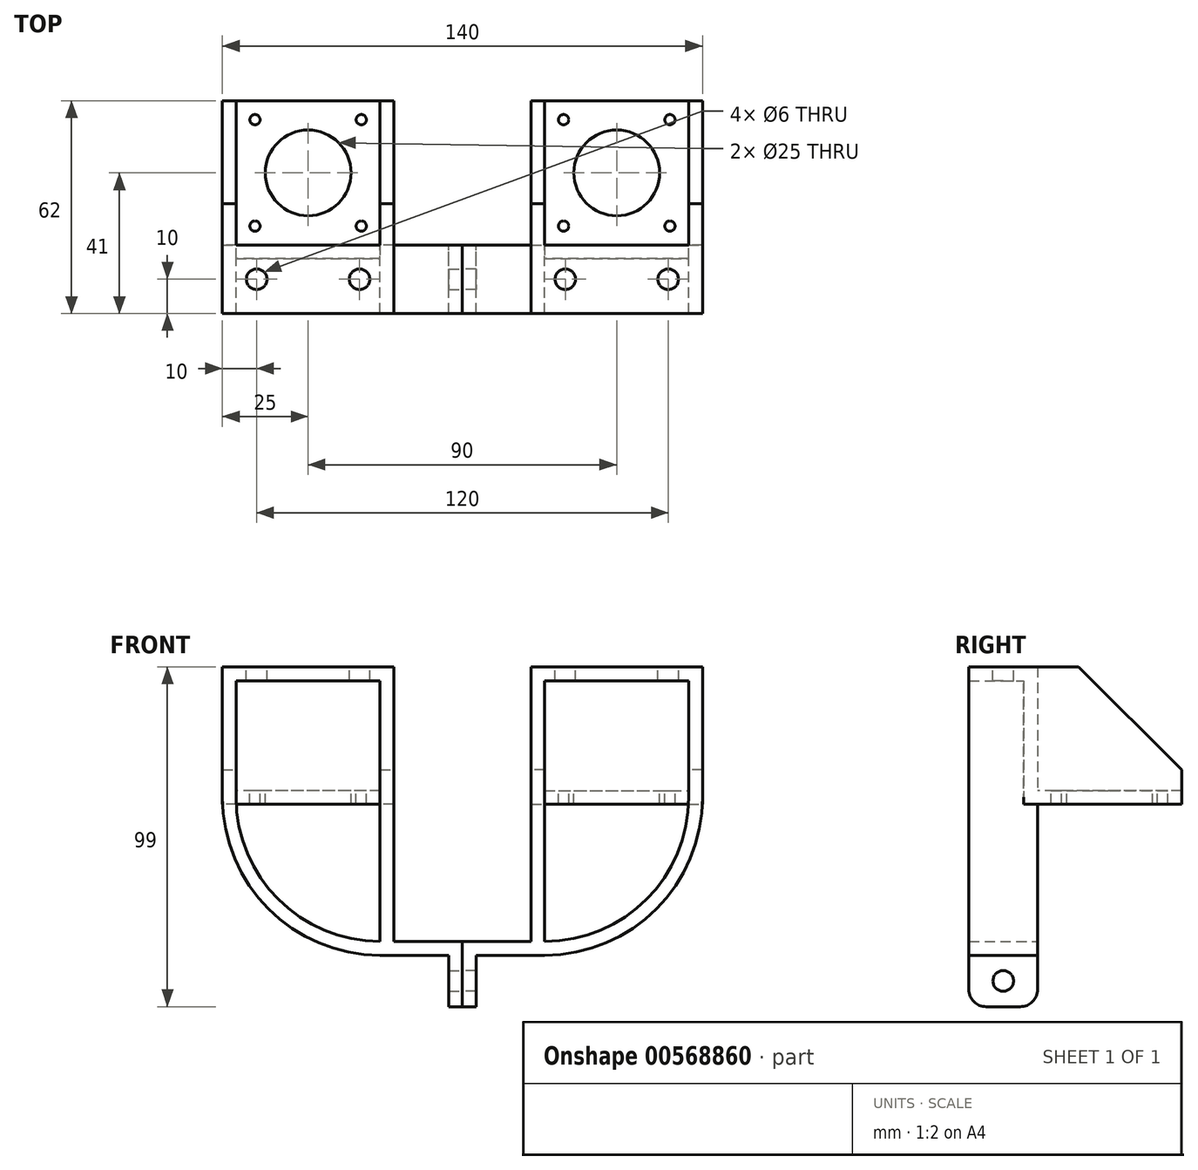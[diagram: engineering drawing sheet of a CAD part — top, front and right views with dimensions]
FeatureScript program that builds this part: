
annotation { "Feature Type Name" : "Feature", "Feature Type Description" : "" }
export const myFeature = defineFeature(function(context is Context, id is Id, definition is map)
    precondition{}
    {
        {
            var Q0;
            Q0=qCreatedBy(makeId("Front.planeOp"),FACE);
            var sketch = newSketch(context, id + "F0", { "sketchPlane" : qUnion([Q0])});
            skLineSegment(sketch, "E0", {"start": v(-16.67, 0) * mm, "end": v(0, 0) * mm, "construction": true});
            skLineSegment(sketch, "E1", {"start": v(0, 0) * mm, "end": v(0, -123.09) * mm, "construction": true});
            skLineSegment(sketch, "E2", {"start": v(-20, 0) * mm, "end": v(-20, -2.5) * mm, "construction": true});
            skLineSegment(sketch, "E3", {"start": v(-20, -2.5) * mm, "end": v(-2.5, -20) * mm, "construction": true});
            skLineSegment(sketch, "E4", {"start": v(-2.5, -20) * mm, "end": v(0, -20) * mm, "construction": true});
            skCircle(sketch, "E5", {"center": v(-6, -50) * mm, "radius": 6 * mm, "construction": true});
            skCircle(sketch, "E6", {"center": v(-6, -50) * mm, "radius": 10 * mm, "construction": true});
            skLineSegment(sketch, "E7", {"start": v(-20, 0) * mm, "end": v(-20, -40) * mm});
            skLineSegment(sketch, "E8", {"start": v(-20, -40) * mm, "end": v(-70, -40) * mm});
            skLineSegment(sketch, "E9", {"start": v(-70, -40) * mm, "end": v(-70, 0) * mm});
            skLineSegment(sketch, "E10", {"start": v(-20, 0) * mm, "end": v(-70, 0) * mm});
            skLineSegment(sketch, "E11.0", {"start": v(-66, -36) * mm, "end": v(-66, 0) * mm});
            skLineSegment(sketch, "E11.1", {"start": v(-24, -36) * mm, "end": v(-66, -36) * mm});
            skLineSegment(sketch, "E11.2", {"start": v(-24, 0) * mm, "end": v(-24, -36) * mm});
            skSolve(sketch);
        }
        {
            var Q0;
            Q0 = qSketchRegion(id + "F0", true);
            extrude(context, id + "F1", {"entities" : qUnion([Q0]), "depth" : 4 * mm, "offsetDistance" : 25 * mm});
        }
        {
            var Q0;
            {var subQ1=sQuery(id+"F0.wireOp",EDGE,"E7");Q0=makeQuery(id+"F0.imprint","IMPRINT",FACE,{"disambiguationData":[TD([[makeQuery(id+"F0.imprint","IMPRINT",EDGE,{"derivedFrom":subQ1}),-1.0]])]});}
            extrude(context, id + "F2", {"entities" : qUnion([Q0]), "operationType" : NewBodyOperationType.ADD, "oppositeDirection" : true, "depth" : 42 * mm, "offsetDistance" : 25 * mm});
        }
        {
            var Q0;
            Q0=qCreatedBy(makeId("Front.planeOp"),FACE);
            var sketch = newSketch(context, id + "F3", { "sketchPlane" : qUnion([Q0])});
            skLineSegment(sketch, "E12.0", {"start": v(-20, 0) * mm, "end": v(-70, 0) * mm});
            skCircle(sketch, "E13.0", {"center": v(-6, -50) * mm, "radius": 10 * mm, "construction": true});
            skCircle(sketch, "E13.1", {"center": v(-6, -50) * mm, "radius": 6 * mm, "construction": true});
            skLineSegment(sketch, "E13.2", {"start": v(0, 0) * mm, "end": v(0, -123.09) * mm, "construction": true});
            skLineSegment(sketch, "E14.0", {"start": v(-16.67, 0) * mm, "end": v(0, 0) * mm, "construction": true});
            skLineSegment(sketch, "E15", {"start": v(-20, 0) * mm, "end": v(-20, -80) * mm});
            skLineSegment(sketch, "E16", {"start": v(-20, -80) * mm, "end": v(0, -80) * mm});
            skLineSegment(sketch, "E17", {"start": v(0, -80) * mm, "end": v(0, -99) * mm});
            skLineSegment(sketch, "E18", {"start": v(-70, -38) * mm, "end": v(-70, 0) * mm});
            skLineSegment(sketch, "E19.0", {"start": v(-24, -4) * mm, "end": v(-24, -80) * mm});
            skLineSegment(sketch, "E19.1", {"start": v(-24, -4) * mm, "end": v(-66, -4) * mm});
            skLineSegment(sketch, "E19.2", {"start": v(-66, -38) * mm, "end": v(-66, -4) * mm});
            skLineSegment(sketch, "E20", {"start": v(-4, -84) * mm, "end": v(-24, -84) * mm});
            skLineSegment(sketch, "E21", {"start": v(-4, -84) * mm, "end": v(-4, -99) * mm});
            skLineSegment(sketch, "E22", {"start": v(-4, -99) * mm, "end": v(0, -99) * mm});
            skArc(sketch, "E23", {"start": v(-66, -38) * mm, "mid": v(-53.7, -67.7) * mm, "end": v(-24, -80) * mm});
            skArc(sketch, "E24", {"start": v(-70, -38) * mm, "mid": v(-56.53, -70.53) * mm, "end": v(-24, -84) * mm});
            skSolve(sketch);
        }
        {
            var Q0;
            Q0 = qSketchRegion(id + "F3", true);
            extrude(context, id + "F4", {"entities" : qUnion([Q0]), "operationType" : NewBodyOperationType.ADD, "depth" : 20 * mm, "offsetDistance" : 25 * mm});
        }
        {
            var Q0;
            {var subQ0=sQuery(id+"F0.wireOp",EDGE,"E10");Q0=makeQuery(id+"F2.opExtrude","CAP_EDGE",EDGE,{"disambiguationData":[OSD([subQ0]),TDD([makeQuery(id+"F0.imprint","IMPRINT",EDGE,{"disambiguationData":[TD([[makeQuery(id+"F0.imprint","INTERSECT",VERTEX,{"derivedFrom":[sQuery(id+"F0.wireOp",EDGE,"E7"),subQ0]}),-1.0]])],"derivedFrom":subQ0})])],"isStart":false});}
            var Q1;
            {var subQ0=sQuery(id+"F0.wireOp",EDGE,"E10");Q1=makeQuery(id+"F2.opExtrude","CAP_EDGE",EDGE,{"disambiguationData":[OSD([subQ0]),TDD([makeQuery(id+"F0.imprint","IMPRINT",EDGE,{"disambiguationData":[TD([[makeQuery(id+"F0.imprint","INTERSECT",VERTEX,{"derivedFrom":[sQuery(id+"F0.wireOp",EDGE,"E9"),subQ0]}),1.0]])],"derivedFrom":subQ0})])],"isStart":false});}
            chamfer(context, id + "F5", {"entities" : qUnion([Q0, Q1]), "width" : 30 * mm, "tangentPropagation" : true});
        }
        {
            var Q0;
            Q0=makeQuery(id+"F4.opExtrude","CAP_EDGE",EDGE,{"disambiguationData":[OSD([sQuery(id+"F3.wireOp",EDGE,"E22")])],"isStart":true});
            var Q1;
            Q1=makeQuery(id+"F4.opExtrude","CAP_EDGE",EDGE,{"disambiguationData":[OSD([sQuery(id+"F3.wireOp",EDGE,"E22")])],"isStart":false});
            fillet(context, id + "F6", {"entities" : qUnion([Q0, Q1]), "radius" : 5 * mm, "tangentPropagation" : true, "allowEdgeOverflow" : false});
        }
        {
            var Q0;
            Q0=qCreatedBy(makeId("Top.planeOp"),FACE);
            var sketch = newSketch(context, id + "F7", { "sketchPlane" : qUnion([Q0])});
            skLineSegment(sketch, "E25.0.0", {"start": v(-66, 0) * mm, "end": v(-66, 12) * mm, "construction": true});
            skLineSegment(sketch, "E25.0.1", {"start": v(-66, 12) * mm, "end": v(-70, 12) * mm, "construction": true});
            skLineSegment(sketch, "E25.0.2", {"start": v(-70, 12) * mm, "end": v(-70, -20) * mm, "construction": true});
            skLineSegment(sketch, "E25.0.3", {"start": v(-70, -20) * mm, "end": v(-20, -20) * mm, "construction": true});
            skLineSegment(sketch, "E25.0.4", {"start": v(-20, -20) * mm, "end": v(-20, 12) * mm, "construction": true});
            skLineSegment(sketch, "E25.0.5", {"start": v(-20, 12) * mm, "end": v(-24, 12) * mm, "construction": true});
            skLineSegment(sketch, "E25.0.6", {"start": v(-24, 12) * mm, "end": v(-24, 0) * mm, "construction": true});
            skLineSegment(sketch, "E25.0.7", {"start": v(-24, 0) * mm, "end": v(-66, 0) * mm, "construction": true});
            skLineSegment(sketch, "E26", {"start": v(-30, 0) * mm, "end": v(-30, -20) * mm, "construction": true});
            skLineSegment(sketch, "E27", {"start": v(-60, 0) * mm, "end": v(-60, -20) * mm, "construction": true});
            skCircle(sketch, "E28", {"center": v(-30, -10) * mm, "radius": 3 * mm});
            skCircle(sketch, "E29", {"center": v(-60, -10) * mm, "radius": 3 * mm});
            skSolve(sketch);
        }
        {
            var Q0;
            Q0 = qSketchRegion(id + "F7", true);
            extrude(context, id + "F8", {"entities" : qUnion([Q0]), "operationType" : NewBodyOperationType.REMOVE, "oppositeDirection" : true, "depth" : 25 * mm, "offsetDistance" : 25 * mm});
        }
        {
            var Q0;
            Q0=qCreatedBy(makeId("Right.planeOp"),FACE);
            var sketch = newSketch(context, id + "F9", { "sketchPlane" : qUnion([Q0])});
            skLineSegment(sketch, "E30.0.0", {"start": v(0, -84) * mm, "end": v(0, -94) * mm, "construction": true});
            skArc(sketch, "E30.0.1", {"start": v(0, -94) * mm, "mid": v(-1.46, -97.54) * mm, "end": v(-5, -99) * mm, "construction": true});
            skLineSegment(sketch, "E30.0.2", {"start": v(-5, -99) * mm, "end": v(-15, -99) * mm, "construction": true});
            skArc(sketch, "E30.0.3", {"start": v(-15, -99) * mm, "mid": v(-18.54, -97.54) * mm, "end": v(-20, -94) * mm, "construction": true});
            skLineSegment(sketch, "E30.0.4", {"start": v(-20, -94) * mm, "end": v(-20, -84) * mm, "construction": true});
            skLineSegment(sketch, "E30.0.5", {"start": v(-20, -84) * mm, "end": v(0, -84) * mm, "construction": true});
            skLineSegment(sketch, "E31", {"start": v(-10, -84) * mm, "end": v(-10, -99) * mm, "construction": true});
            skCircle(sketch, "E32", {"center": v(-10, -91.5) * mm, "radius": 3 * mm});
            skSolve(sketch);
        }
        {
            var Q0;
            Q0 = qSketchRegion(id + "F9", true);
            extrude(context, id + "F10", {"entities" : qUnion([Q0]), "operationType" : NewBodyOperationType.REMOVE, "oppositeDirection" : true, "depth" : 25 * mm, "offsetDistance" : 25 * mm});
        }
        {
            var Q0;
            Q0=qCreatedBy(makeId("Top.planeOp"),FACE);
            var sketch = newSketch(context, id + "F11", { "sketchPlane" : qUnion([Q0])});
            skLineSegment(sketch, "E33.0.0", {"start": v(-66, 0) * mm, "end": v(-24, 0) * mm, "construction": true});
            skLineSegment(sketch, "E33.0.1", {"start": v(-24, 0) * mm, "end": v(-24, 42) * mm, "construction": true});
            skLineSegment(sketch, "E33.0.2", {"start": v(-24, 42) * mm, "end": v(-66, 42) * mm, "construction": true});
            skLineSegment(sketch, "E33.0.3", {"start": v(-66, 42) * mm, "end": v(-66, 0) * mm, "construction": true});
            skLineSegment(sketch, "E34", {"start": v(-66, 42) * mm, "end": v(-24, 0) * mm, "construction": true});
            skLineSegment(sketch, "E35", {"start": v(-66, 0) * mm, "end": v(-24, 42) * mm, "construction": true});
            skCircle(sketch, "E36", {"center": v(-45, 21) * mm, "radius": 12.5 * mm});
            skCircle(sketch, "E37", {"center": v(-60.5, 36.5) * mm, "radius": 1.5 * mm});
            skCircle(sketch, "E38", {"center": v(-29.5, 36.5) * mm, "radius": 1.5 * mm});
            skCircle(sketch, "E39", {"center": v(-29.5, 5.5) * mm, "radius": 1.5 * mm});
            skCircle(sketch, "E40", {"center": v(-60.5, 5.5) * mm, "radius": 1.5 * mm});
            skSolve(sketch);
        }
        {
            var Q0;
            Q0 = qSketchRegion(id + "F11", true);
            extrude(context, id + "F12", {"entities" : qUnion([Q0]), "operationType" : NewBodyOperationType.REMOVE, "oppositeDirection" : true, "depth" : 50 * mm, "offsetDistance" : 25 * mm});
        }
        {
            var Q0;
            Q0=makeQuery(id+"F1.opExtrude","SWEPT_BODY",BODY,{"disambiguationData":[OSD([sQuery(id+"F0.wireOp",EDGE,"E7"),sQuery(id+"F0.wireOp",EDGE,"E8"),sQuery(id+"F0.wireOp",EDGE,"E9"),sQuery(id+"F0.wireOp",EDGE,"E10")])]});
            var Q1;
            Q1=qCreatedBy(makeId("Right.planeOp"),FACE);
            mirror(context, id + "F13", {"entities" : qUnion([Q0]), "mirrorPlane" : qUnion([Q1])});
        }
    });
